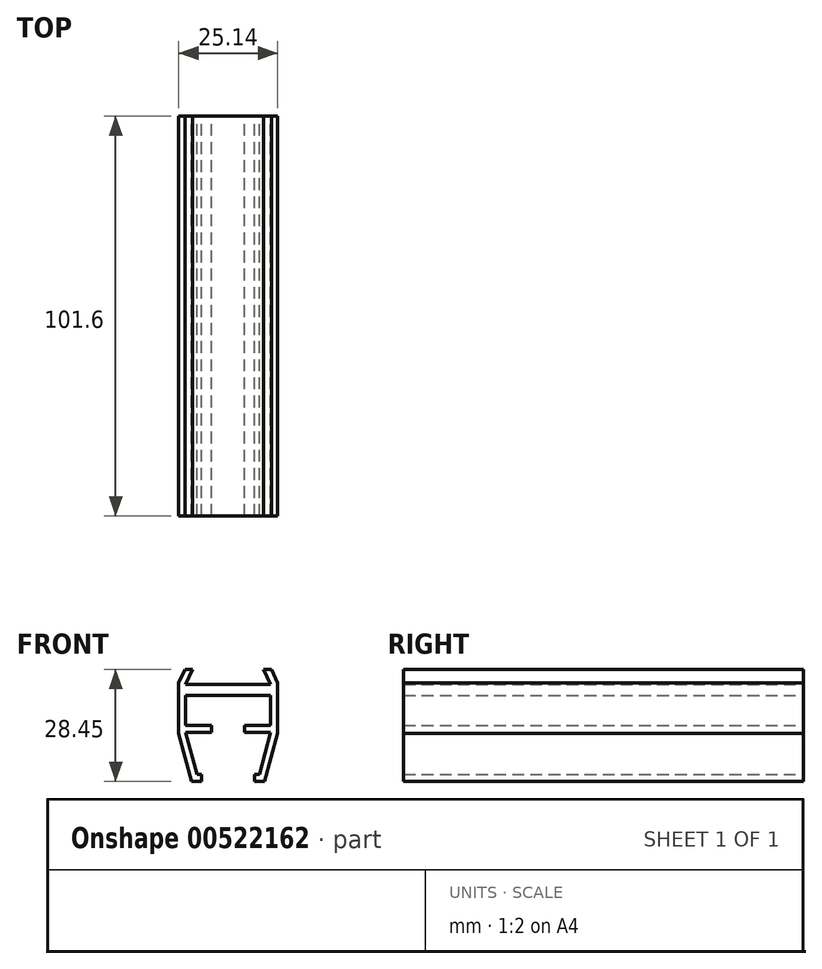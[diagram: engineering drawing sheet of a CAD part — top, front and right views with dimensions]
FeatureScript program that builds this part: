
annotation { "Feature Type Name" : "Feature", "Feature Type Description" : "" }
export const myFeature = defineFeature(function(context is Context, id is Id, definition is map)
    precondition{}
    {
        {
            var Q0;
            Q0=qCreatedBy(makeId("Front.planeOp"),FACE);
            var sketch = newSketch(context, id + "F0", { "sketchPlane" : qUnion([Q0])});
            skLineSegment(sketch, "E0", {"start": v(10.98, 28.45) * mm, "end": v(12.57, 25.03) * mm});
            skLineSegment(sketch, "E1", {"start": v(12.57, 25.03) * mm, "end": v(12.57, 12.21) * mm});
            skLineSegment(sketch, "E2", {"start": v(12.57, 12.21) * mm, "end": v(9.3, 0) * mm});
            skLineSegment(sketch, "E3", {"start": v(9.3, 0) * mm, "end": v(6.73, 0) * mm});
            skLineSegment(sketch, "E4", {"start": v(6.73, 0) * mm, "end": v(6.73, 1.78) * mm});
            skLineSegment(sketch, "E5", {"start": v(6.73, 1.78) * mm, "end": v(7.94, 1.78) * mm});
            skLineSegment(sketch, "E6", {"start": v(7.94, 1.78) * mm, "end": v(10.8, 12.45) * mm});
            skLineSegment(sketch, "E7", {"start": v(10.8, 12.45) * mm, "end": v(4.2, 12.45) * mm});
            skLineSegment(sketch, "E8", {"start": v(4.2, 12.45) * mm, "end": v(4.2, 14.22) * mm});
            skLineSegment(sketch, "E9", {"start": v(4.2, 14.22) * mm, "end": v(10.8, 14.22) * mm});
            skLineSegment(sketch, "E10", {"start": v(10.8, 14.22) * mm, "end": v(10.8, 21.84) * mm});
            skLineSegment(sketch, "E11", {"start": v(10.8, 21.84) * mm, "end": v(0, 21.84) * mm});
            skLineSegment(sketch, "E12", {"start": v(0, 21.84) * mm, "end": v(0, 24.64) * mm});
            skLineSegment(sketch, "E13", {"start": v(0, 24.64) * mm, "end": v(10.8, 24.64) * mm});
            skLineSegment(sketch, "E14", {"start": v(10.8, 24.64) * mm, "end": v(9.02, 28.45) * mm});
            skLineSegment(sketch, "E15", {"start": v(9.02, 28.45) * mm, "end": v(10.98, 28.45) * mm});
            skLineSegment(sketch, "E16.MirrorCS", {"start": v(-9.02, 28.45) * mm, "end": v(-10.98, 28.45) * mm});
            skLineSegment(sketch, "E17.MirrorCS", {"start": v(-6.73, 1.78) * mm, "end": v(-7.94, 1.78) * mm});
            skLineSegment(sketch, "E18.MirrorCS", {"start": v(-4.2, 12.45) * mm, "end": v(-4.2, 14.22) * mm});
            skLineSegment(sketch, "E19.MirrorCS", {"start": v(-6.73, 0) * mm, "end": v(-6.73, 1.78) * mm});
            skLineSegment(sketch, "E20.MirrorCS", {"start": v(-10.8, 14.22) * mm, "end": v(-10.8, 21.84) * mm});
            skLineSegment(sketch, "E21.MirrorCS", {"start": v(-10.8, 21.84) * mm, "end": v(0, 21.84) * mm});
            skLineSegment(sketch, "E22.MirrorCS", {"start": v(0, 24.64) * mm, "end": v(-10.8, 24.64) * mm});
            skLineSegment(sketch, "E23.MirrorCS", {"start": v(-10.98, 28.45) * mm, "end": v(-12.57, 25.03) * mm});
            skLineSegment(sketch, "E24.MirrorCS", {"start": v(-12.57, 25.03) * mm, "end": v(-12.57, 12.21) * mm});
            skLineSegment(sketch, "E25.MirrorCS", {"start": v(-12.57, 12.21) * mm, "end": v(-9.3, 0) * mm});
            skLineSegment(sketch, "E26.MirrorCS", {"start": v(-10.8, 24.64) * mm, "end": v(-9.02, 28.45) * mm});
            skLineSegment(sketch, "E27.MirrorCS", {"start": v(-7.94, 1.78) * mm, "end": v(-10.8, 12.45) * mm});
            skLineSegment(sketch, "E28.MirrorCS", {"start": v(-9.3, 0) * mm, "end": v(-6.73, 0) * mm});
            skLineSegment(sketch, "E29.MirrorCS", {"start": v(-10.8, 12.45) * mm, "end": v(-4.2, 12.45) * mm});
            skLineSegment(sketch, "E30.MirrorCS", {"start": v(-4.2, 14.22) * mm, "end": v(-10.8, 14.22) * mm});
            skSolve(sketch);
        }
        {
            var Q0;
            Q0 = qSketchRegion(id + "F0", true);
            extrude(context, id + "F1", {"entities" : qUnion([Q0]), "depth" : 101.6 * mm, "offsetDistance" : 25.4 * mm});
        }
    });
